# Revit family: AAC12
name_source: partatom
category: Furniture
revit_build: Autodesk Revit 2016 (Build: 20161004_0715(x64)
units: mm (PartAtom-declared; Revit-internal decimal feet)

## family parameters
Always vertical = Yes
Cut with Voids When Loaded = No
OmniClass Number = 23.40.20.00
OmniClass Title = General Furniture and Specialties
Room Calculation Point = No
Shared = No
Work Plane-Based = No

## types (1)
- AAC12
    Base = HAY Matt laquered Oak Vertical
    Depth = 50cm - 19.88inch
    Description = Uncluttered, pared-back chair with solid wooden base and gently curved polypropylene shell. Equally suitable for dining tables, conference tables, offices or public spaces.
    Design = Hee Welling & HAY
    Gliders = HAY White Gliders
    Height = 78.50cm - 30.91inch
    Manufacturer = HAY
    Model = AAC 12 Solid wood legs
    Optional Upholstery = Seat upholstery, Front upholstery
    Price = Contact HAY or visit hay.dk
    Seat Height = 46cm - 18.11inch
    Shell = HAY Black Polypropylene
    Strength, durability and safety = EN 16139:2013 L2
    Type Comments = Injection moulded solid-coloured polypropylene shell without armrest. Front upholstery or fixed seat cushion with 10 mm foam is optional.
    URL = http://hay.dk
    Upholstery fabric = Available in a large selection of standard fabrics and leathers.
    Variations = Available in a large selection of shell colours and base finishes. Other base options are:  4-leg steel base, swivel base, wheel base, sled base and moulded plywood legs. Shell is also available with armrest.
    Width = 51cm - 20.08inch

## geometry (parser evidence)
native form markers: Sweep x3
no freeform markers — native parametric forms only
